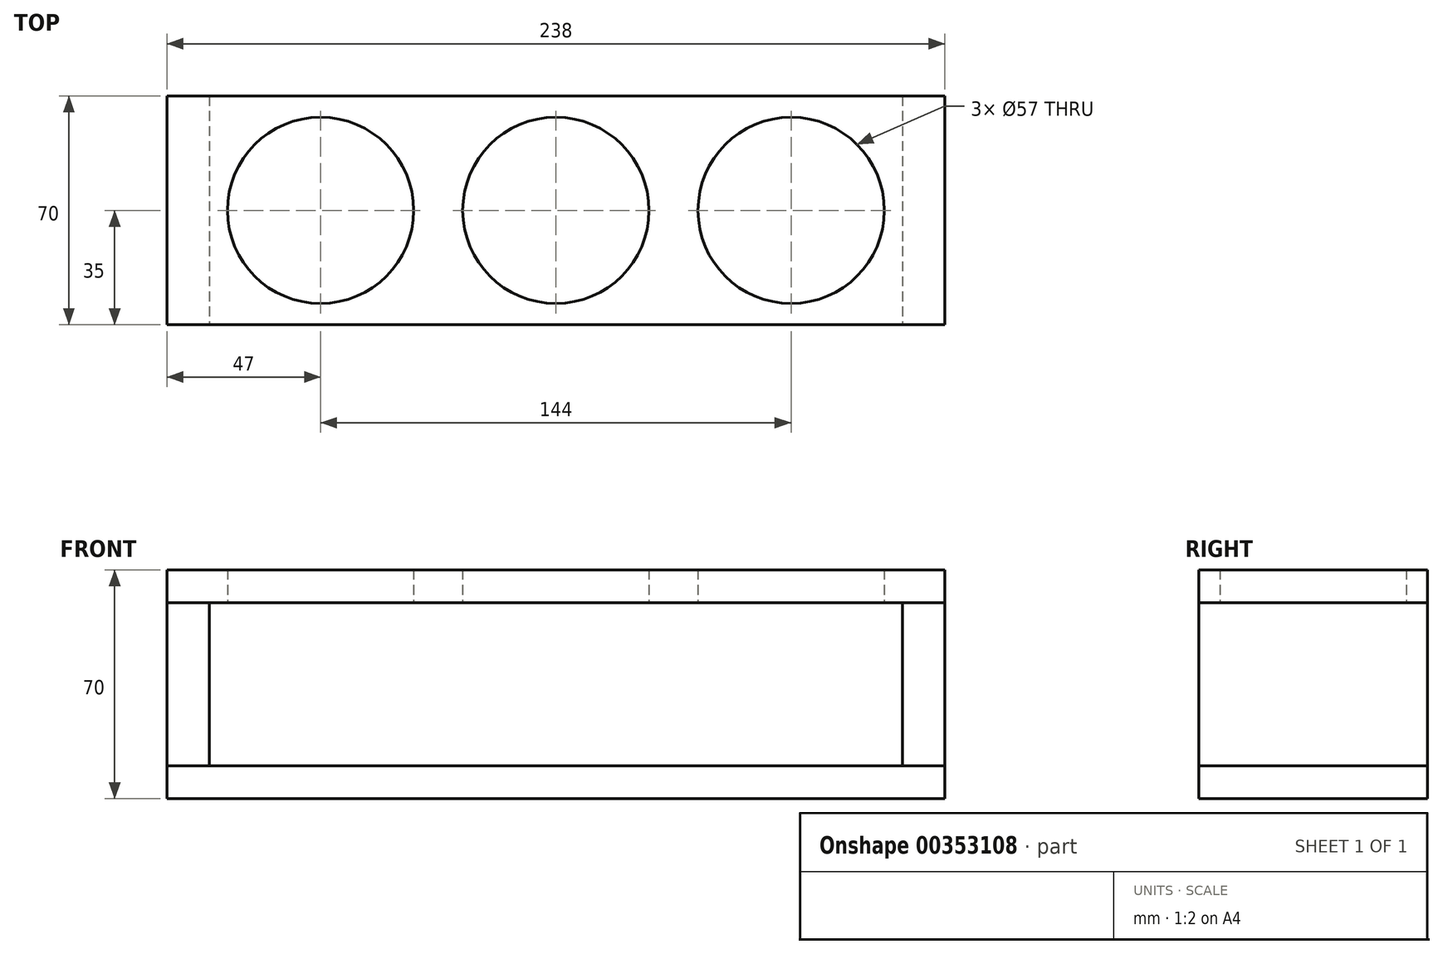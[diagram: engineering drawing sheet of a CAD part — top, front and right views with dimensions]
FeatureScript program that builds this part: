
annotation { "Feature Type Name" : "Feature", "Feature Type Description" : "" }
export const myFeature = defineFeature(function(context is Context, id is Id, definition is map)
    precondition{}
    {
        {
            var Q0;
            Q0=qCreatedBy(makeId("Top.planeOp"),FACE);
            var sketch = newSketch(context, id + "F0", { "sketchPlane" : qUnion([Q0])});
            skLineSegment(sketch, "E0.bottom", {"start": v(119, -35) * mm, "end": v(-119, -35) * mm});
            skLineSegment(sketch, "E0.top", {"start": v(119, 35) * mm, "end": v(-119, 35) * mm});
            skLineSegment(sketch, "E0.left", {"start": v(119, -35) * mm, "end": v(119, 35) * mm});
            skLineSegment(sketch, "E0.right", {"start": v(-119, -35) * mm, "end": v(-119, 35) * mm});
            skPoint(sketch, "E0.middle", {"position": v(0, 0) * mm});
            skSolve(sketch);
        }
        {
            var Q0;
            Q0=qSketchRegion(id+"F0",true);
            extrude(context, id + "F1", {"entities" : qUnion([Q0]), "depth" : 10 * mm});
        }
        {
            var Q0;
            Q0=makeQuery(id+"F1.opExtrude","CAP_FACE",FACE,{"disambiguationData":[OSD([sQuery(id+"F0.wireOp",EDGE,"E0.bottom"),sQuery(id+"F0.wireOp",EDGE,"E0.top"),sQuery(id+"F0.wireOp",EDGE,"E0.left"),sQuery(id+"F0.wireOp",EDGE,"E0.right")])],"isStart":false});
            cPlane(context, id + "F2", {"entities" : qUnion([Q0]), "cplaneType" : CPlaneType.OFFSET, "offset" : 50 * mm, "width" : 150 * mm, "height" : 150 * mm});
        }
        {
            var Q0;
            Q0=qCreatedBy(id+"F2.planeOp",FACE);
            var sketch = newSketch(context, id + "F3", { "sketchPlane" : qUnion([Q0])});
            skLineSegment(sketch, "E1.0", {"start": v(119, -35) * mm, "end": v(-119, -35) * mm});
            skLineSegment(sketch, "E1.1", {"start": v(119, 35) * mm, "end": v(-119, 35) * mm});
            skLineSegment(sketch, "E1.2", {"start": v(119, -35) * mm, "end": v(119, 35) * mm});
            skLineSegment(sketch, "E1.3", {"start": v(-119, -35) * mm, "end": v(-119, 35) * mm});
            skPoint(sketch, "E1.4", {"position": v(0, 0) * mm});
            skLineSegment(sketch, "E2", {"start": v(-119, 0) * mm, "end": v(119, 0) * mm, "construction": true});
            skCircle(sketch, "E3", {"center": v(-72, 0) * mm, "radius": 28.5 * mm});
            skCircle(sketch, "E4.1.0.0", {"center": v(0, 0) * mm, "radius": 28.5 * mm});
            skCircle(sketch, "E4.2.0.0", {"center": v(72, 0) * mm, "radius": 28.5 * mm});
            skLineSegment(sketch, "E4.direction1", {"start": v(-72, 0) * mm, "end": v(0, 0) * mm, "construction": true});
            skSolve(sketch);
        }
        {
            var Q0;
            Q0=qSketchRegion(id+"F3",true);
            extrude(context, id + "F4", {"entities" : qUnion([Q0]), "depth" : 10 * mm});
        }
        {
            var Q0;
            Q0=makeQuery(id+"F1.opExtrude","CAP_FACE",FACE,{"disambiguationData":[OSD([sQuery(id+"F0.wireOp",EDGE,"E0.bottom"),sQuery(id+"F0.wireOp",EDGE,"E0.top"),sQuery(id+"F0.wireOp",EDGE,"E0.left"),sQuery(id+"F0.wireOp",EDGE,"E0.right")])],"isStart":false});
            var sketch = newSketch(context, id + "F5", { "sketchPlane" : qUnion([Q0])});
            skLineSegment(sketch, "E5.bottom", {"start": v(-119, 35) * mm, "end": v(-106, 35) * mm});
            skLineSegment(sketch, "E5.top", {"start": v(-119, -35) * mm, "end": v(-106, -35) * mm});
            skLineSegment(sketch, "E5.left", {"start": v(-119, 35) * mm, "end": v(-119, -35) * mm});
            skLineSegment(sketch, "E5.right", {"start": v(-106, 35) * mm, "end": v(-106, -35) * mm});
            skLineSegment(sketch, "E6.bottom", {"start": v(119, 35) * mm, "end": v(106, 35) * mm});
            skLineSegment(sketch, "E6.top", {"start": v(119, -35) * mm, "end": v(106, -35) * mm});
            skLineSegment(sketch, "E6.left", {"start": v(119, 35) * mm, "end": v(119, -35) * mm});
            skLineSegment(sketch, "E6.right", {"start": v(106, 35) * mm, "end": v(106, -35) * mm});
            skSolve(sketch);
        }
        {
            var Q0;
            Q0 = qSketchRegion(id + "F5", true);
            var Q1;
            Q1=qCreatedBy(id+"F2.planeOp",FACE);
            extrude(context, id + "F6", {"entities" : qUnion([Q0]), "endBound" : BoundingType.UP_TO_SURFACE, "endBoundEntityFace" : qUnion([Q1]), "depth" : 25 * mm});
        }
    });
